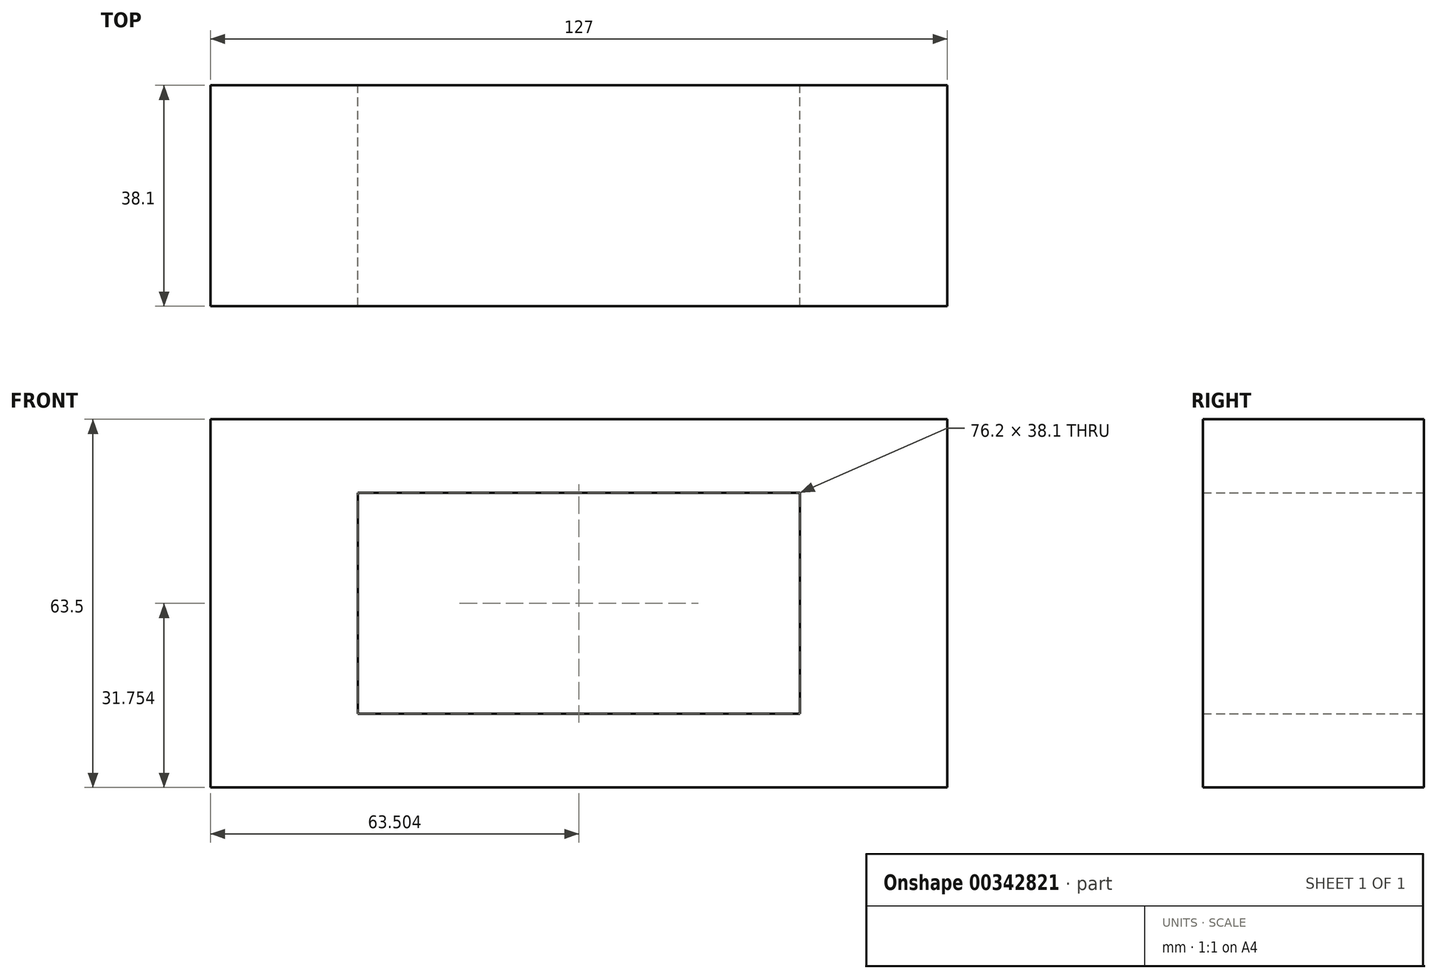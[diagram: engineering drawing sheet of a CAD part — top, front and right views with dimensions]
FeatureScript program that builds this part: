
annotation { "Feature Type Name" : "Feature", "Feature Type Description" : "" }
export const myFeature = defineFeature(function(context is Context, id is Id, definition is map)
    precondition{}
    {
        {
            var Q0;
            Q0=qCreatedBy(makeId("Front.planeOp"),FACE);
            var sketch = newSketch(context, id + "F0", { "sketchPlane" : qUnion([Q0])});
            skLineSegment(sketch, "E0", {"start": v(-60.89, 34.12) * mm, "end": v(66.11, 34.12) * mm});
            skLineSegment(sketch, "E1", {"start": v(66.11, 34.12) * mm, "end": v(66.11, -29.38) * mm});
            skLineSegment(sketch, "E2", {"start": v(66.11, -29.38) * mm, "end": v(-60.89, -29.38) * mm});
            skLineSegment(sketch, "E3", {"start": v(-60.89, -29.38) * mm, "end": v(-60.89, 34.12) * mm});
            skLineSegment(sketch, "E4", {"start": v(-35.49, 21.42) * mm, "end": v(-35.49, -16.68) * mm});
            skLineSegment(sketch, "E5", {"start": v(-35.49, 21.42) * mm, "end": v(40.71, 21.42) * mm});
            skLineSegment(sketch, "E6", {"start": v(40.71, 21.42) * mm, "end": v(40.71, -16.68) * mm});
            skLineSegment(sketch, "E7", {"start": v(40.71, -16.68) * mm, "end": v(-35.49, -16.68) * mm});
            skSolve(sketch);
        }
        {
            var Q0;
            Q0=makeQuery(id+"F0.imprint","IMPRINT",FACE,{"disambiguationData":[TD([[makeQuery(id+"F0.imprint","IMPRINT",EDGE,{"derivedFrom":sQuery(id+"F0.wireOp",EDGE,"E0")}),-1.0]])]});
            extrude(context, id + "F1", {"entities" : qUnion([Q0]), "depth" : 38.1 * mm});
        }
    });
